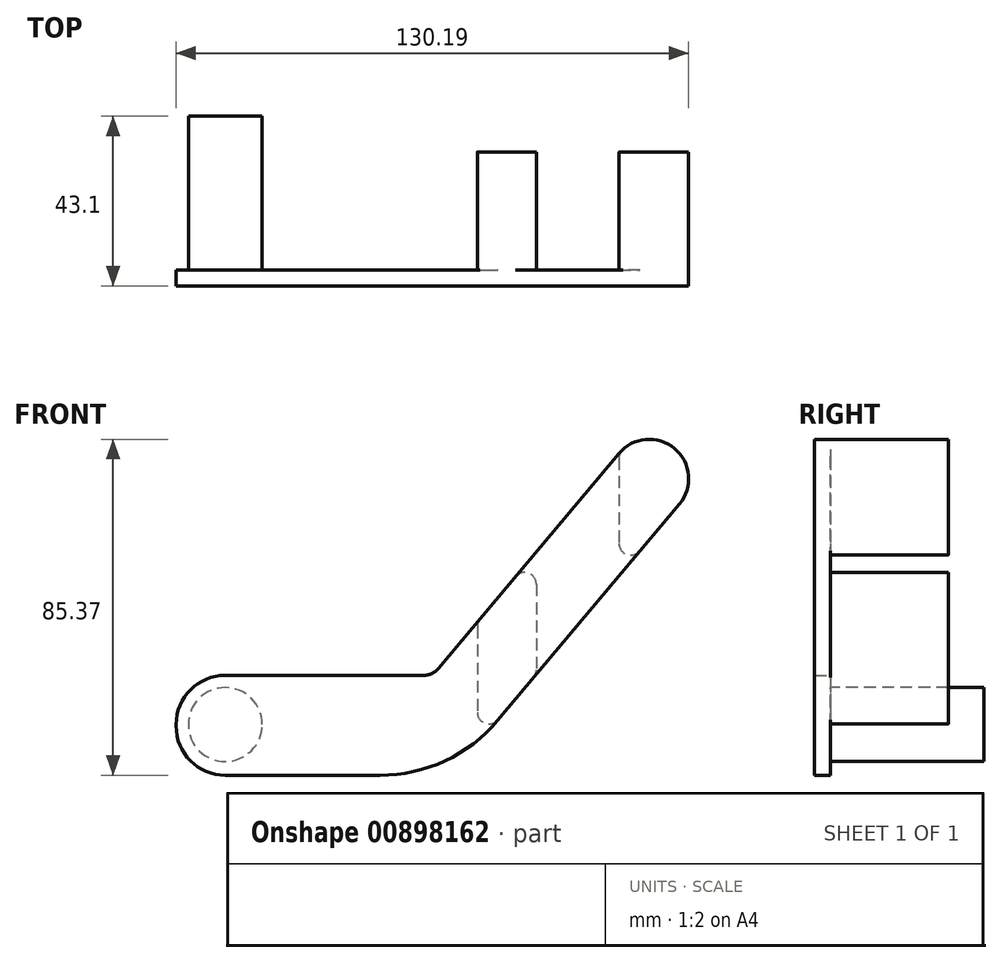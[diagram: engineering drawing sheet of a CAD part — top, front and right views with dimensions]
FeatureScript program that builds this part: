
annotation { "Feature Type Name" : "Feature", "Feature Type Description" : "" }
export const myFeature = defineFeature(function(context is Context, id is Id, definition is map)
    precondition{}
    {
        {
            var Q0;
            Q0=qCreatedBy(makeId("Front.planeOp"),FACE);
            var sketch = newSketch(context, id + "F0", { "sketchPlane" : qUnion([Q0])});
            skLineSegment(sketch, "E0.bottom", {"start": v(0, 0) * mm, "end": v(-70, 0) * mm});
            skLineSegment(sketch, "E0.top", {"start": v(-4.8, 25.4) * mm, "end": v(-70, 25.4) * mm});
            skLineSegment(sketch, "E0.right", {"start": v(-70, 0) * mm, "end": v(-70, 25.4) * mm});
            skLineSegment(sketch, "E1", {"start": v(-4.8, 25.4) * mm, "end": v(48.96, 89.46) * mm});
            skLineSegment(sketch, "E2", {"start": v(48.96, 89.46) * mm, "end": v(64.28, 76.6) * mm});
            skLineSegment(sketch, "E3", {"start": v(64.28, 76.6) * mm, "end": v(0, 0) * mm});
            skSolve(sketch);
        }
        {
            var Q0;
            Q0 = qSketchRegion(id + "F0", true);
            extrude(context, id + "F1", {"entities" : qUnion([Q0]), "depth" : 4 * mm, "offsetDistance" : 25 * mm});
        }
        {
            var Q0;
            Q0=makeQuery(id+"F1.opExtrude","SWEPT_EDGE",EDGE,{"disambiguationData":[OSD([sQuery(id+"F0.wireOp",EDGE,"E2"),sQuery(id+"F0.wireOp",EDGE,"E3")])]});
            var Q1;
            Q1=makeQuery(id+"F1.opExtrude","SWEPT_EDGE",EDGE,{"disambiguationData":[OSD([sQuery(id+"F0.wireOp",EDGE,"E1"),sQuery(id+"F0.wireOp",EDGE,"E2")])]});
            fillet(context, id + "F2", {"entities" : qUnion([Q0, Q1]), "radius" : 10 * mm, "tangentPropagation" : true, "allowEdgeOverflow" : false});
        }
        {
            var Q0;
            Q0=makeQuery(id+"F1.opExtrude","SWEPT_EDGE",EDGE,{"disambiguationData":[OSD([sQuery(id+"F0.wireOp",EDGE,"E0.bottom"),sQuery(id+"F0.wireOp",EDGE,"E0.right")])]});
            var Q1;
            Q1=makeQuery(id+"F1.opExtrude","SWEPT_EDGE",EDGE,{"disambiguationData":[OSD([sQuery(id+"F0.wireOp",EDGE,"E0.top"),sQuery(id+"F0.wireOp",EDGE,"E0.right")])]});
            fillet(context, id + "F3", {"entities" : qUnion([Q0, Q1]), "radius" : 12.5 * mm, "tangentPropagation" : true, "allowEdgeOverflow" : false});
        }
        {
            var Q0;
            Q0=makeQuery(id+"F1.opExtrude","CAP_FACE",FACE,{"disambiguationData":[OSD([sQuery(id+"F0.wireOp",EDGE,"E0.bottom"),sQuery(id+"F0.wireOp",EDGE,"E0.top"),sQuery(id+"F0.wireOp",EDGE,"E0.right"),sQuery(id+"F0.wireOp",EDGE,"E1"),sQuery(id+"F0.wireOp",EDGE,"E2"),sQuery(id+"F0.wireOp",EDGE,"E3")])],"isStart":false});
            var sketch = newSketch(context, id + "F4", { "sketchPlane" : qUnion([Q0])});
            skCircle(sketch, "E4", {"center": v(-57.5, 12.9) * mm, "radius": 9.38 * mm});
            skSolve(sketch);
        }
        {
            var Q0;
            Q0=makeQuery(id+"F1.opExtrude","CAP_FACE",FACE,{"disambiguationData":[OSD([sQuery(id+"F0.wireOp",EDGE,"E0.bottom"),sQuery(id+"F0.wireOp",EDGE,"E0.top"),sQuery(id+"F0.wireOp",EDGE,"E0.right"),sQuery(id+"F0.wireOp",EDGE,"E1"),sQuery(id+"F0.wireOp",EDGE,"E2"),sQuery(id+"F0.wireOp",EDGE,"E3")])],"isStart":true});
            var sketch = newSketch(context, id + "F5", { "sketchPlane" : qUnion([Q0])});
            skLineSegment(sketch, "E5", {"start": v(-42.53, 81.8) * mm, "end": v(-42.53, 50.69) * mm});
            skLineSegment(sketch, "E6", {"start": v(-21.53, 56.77) * mm, "end": v(-21.53, 25.66) * mm});
            skLineSegment(sketch, "E7", {"start": v(-6.53, 38.9) * mm, "end": v(-6.53, 7.78) * mm});
            skSolve(sketch);
        }
        {
            var Q0;
            Q0 = qSketchRegion(id + "F5", true);
            var Q1;
            {var subQ0=sQuery(id+"F5.wireOp",EDGE,"E5");Q1=makeQuery(id+"F5.imprint","IMPRINT",FACE,{"disambiguationData":[TD([[makeQuery(id+"F5.imprint","IMPRINT",EDGE,{"derivedFrom":subQ0}),-1.0]])]});}
            var Q2;
            {var subQ0=sQuery(id+"F5.wireOp",EDGE,"E6");Q2=makeQuery(id+"F5.imprint","IMPRINT",FACE,{"disambiguationData":[TD([[makeQuery(id+"F5.imprint","IMPRINT",EDGE,{"derivedFrom":subQ0}),1.0]])]});}
            extrude(context, id + "F6", {"entities" : qUnion([Q0, Q1, Q2]), "operationType" : NewBodyOperationType.ADD, "depth" : 30 * mm, "offsetDistance" : 25 * mm});
        }
        {
            var Q0;
            Q0=makeQuery(id+"F4.imprint","IMPRINT",FACE,{"disambiguationData":[TD([[makeQuery(id+"F4.imprint","IMPRINT",EDGE,{"derivedFrom":sQuery(id+"F4.wireOp",EDGE,"E4")}),1.0]])]});
            extrude(context, id + "F7", {"entities" : qUnion([Q0]), "operationType" : NewBodyOperationType.ADD, "oppositeDirection" : true, "depth" : 43.1 * mm, "offsetDistance" : 25 * mm});
        }
        {
            var Q0;
            Q0=makeQuery(id+"F6.opExtrude","SWEPT_EDGE",EDGE,{"disambiguationData":[OSD([sQuery(id+"F0.wireOp",EDGE,"E1"),sQuery(id+"F5.wireOp",EDGE,"E6")])]});
            var Q1;
            Q1=makeQuery(id+"F6.opExtrude","SWEPT_EDGE",EDGE,{"disambiguationData":[OSD([sQuery(id+"F0.wireOp",EDGE,"E3"),sQuery(id+"F5.wireOp",EDGE,"E6")])]});
            var Q2;
            Q2=makeQuery(id+"F6.opExtrude","SWEPT_EDGE",EDGE,{"disambiguationData":[OSD([sQuery(id+"F0.wireOp",EDGE,"E3"),sQuery(id+"F5.wireOp",EDGE,"E7")])]});
            var Q3;
            Q3=makeQuery(id+"F6.opExtrude","SWEPT_EDGE",EDGE,{"disambiguationData":[OSD([sQuery(id+"F0.wireOp",EDGE,"E1"),sQuery(id+"F5.wireOp",EDGE,"E7")])]});
            var Q4;
            Q4=makeQuery(id+"F6.opExtrude","SWEPT_EDGE",EDGE,{"disambiguationData":[OSD([sQuery(id+"F0.wireOp",EDGE,"E0.bottom"),sQuery(id+"F0.wireOp",EDGE,"E0.top"),sQuery(id+"F0.wireOp",EDGE,"E0.right"),sQuery(id+"F0.wireOp",EDGE,"E1"),sQuery(id+"F0.wireOp",EDGE,"E2"),sQuery(id+"F0.wireOp",EDGE,"E3"),sQuery(id+"F5.wireOp",EDGE,"E5")])]});
            var Q5;
            Q5=makeQuery(id+"F6.opExtrude","SWEPT_EDGE",EDGE,{"disambiguationData":[OSD([sQuery(id+"F0.wireOp",EDGE,"E3"),sQuery(id+"F5.wireOp",EDGE,"E5")])]});
            fillet(context, id + "F8", {"entities" : qUnion([Q0, Q1, Q2, Q3, Q4, Q5]), "radius" : 3 * mm, "tangentPropagation" : true, "allowEdgeOverflow" : false});
        }
        {
            var Q0;
            Q0=makeQuery(id+"F1.opExtrude","SWEPT_EDGE",EDGE,{"disambiguationData":[OSD([sQuery(id+"F0.wireOp",EDGE,"E0.bottom"),sQuery(id+"F0.wireOp",EDGE,"E3")])]});
            fillet(context, id + "F9", {"entities" : qUnion([Q0]), "radius" : 39 * mm, "tangentPropagation" : true, "allowEdgeOverflow" : false});
        }
        {
            var Q0;
            Q0=makeQuery(id+"F1.opExtrude","SWEPT_EDGE",EDGE,{"disambiguationData":[OSD([sQuery(id+"F0.wireOp",EDGE,"E0.top"),sQuery(id+"F0.wireOp",EDGE,"E1")])]});
            fillet(context, id + "F10", {"entities" : qUnion([Q0]), "radius" : 5 * mm, "tangentPropagation" : true, "allowEdgeOverflow" : false});
        }
    });
